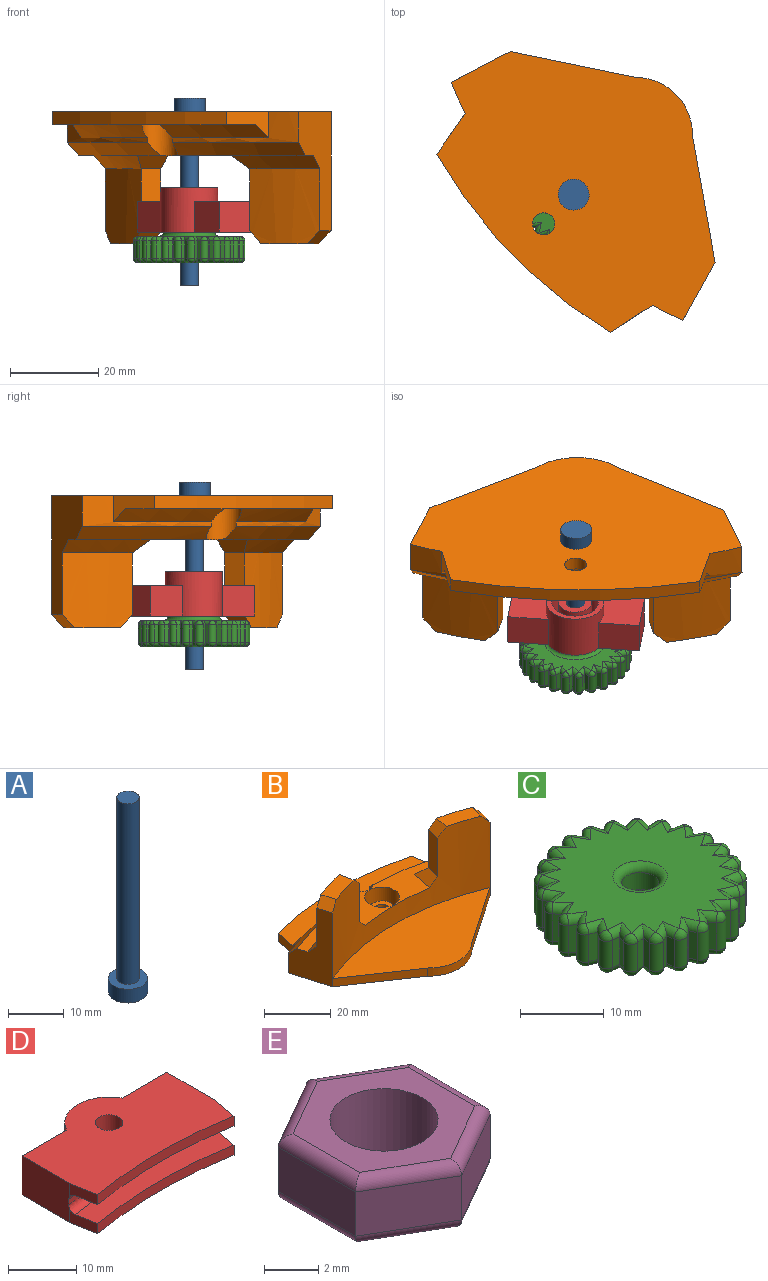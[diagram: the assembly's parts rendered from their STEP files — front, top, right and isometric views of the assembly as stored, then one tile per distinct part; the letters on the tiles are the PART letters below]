
ASSEMBLY  parts=5 mates=4
PART A: 5 faces, bbox 7x7x42.5 mm
  f0: cylinder r=2mm len=39.5mm, axis (0,0,-1), area 496.4mm2, adj f3,f4
  f1: cylinder r=3.5mm len=7mm, axis (0,0,1), area 66mm2, adj f2,f3
  f2: plane 7x7mm, normal (0,0,-1), area 38.5mm2, adj f1
  f3: plane 7x7mm, normal (0,0,1), area 25.9mm2, adj f0,f1
  f4: plane 4x4mm, normal (0,0,1), area 12.6mm2, adj f0
PART B: 40 faces, bbox 75.9x52x30 mm
  f0: cylinder r=5.25mm len=10.5mm, axis (0,0,-1), area 230.9mm2, adj f3,f26
  f1: cylinder r=2mm len=6mm, axis (0,0,-1), area 75.4mm2, adj f17,f27
  f2: cylinder r=3.75mm len=7.5mm, axis (0,0,-1), area 70.7mm2, adj f26,f27
  f3: plane 73.58x13.09mm, normal (0,0,1), area 429.3mm2, adj f0,f7,f11,f18,f19,f30,f31,f36
  f4: plane 66.65x27mm, normal (0,0,1), area 1048.8mm2, adj f8,f9,f10,f18
  f5: plane 11.08x6.03mm, normal (-0.98,0.19,0), area 38.9mm2, adj f6,f14,f16,f17,f28
  f6: cylinder r=100mm len=33.66mm, axis (0,0,-1), area 80.9mm2, adj f5,f7,f17,f19,f28,f31
  f7: plane 27.01x14.45mm, normal (-0.96,-0.29,0), area 240.5mm2, adj f3,f6,f8,f17,f18,f24,f31,f32
  f8: plane 24.01x16.26mm, normal (-0.56,-0.83,0), area 87mm2, adj f4,f7,f9,f17
  f9: cylinder r=13mm len=18.64mm, axis (0,0,-1), area 62.3mm2, adj f4,f8,f10,f17
  f10: plane 24.01x16.26mm, normal (0.56,-0.83,0), area 87mm2, adj f4,f9,f11,f17
  f11: plane 27.01x14.45mm, normal (0.96,-0.29,0), area 240.5mm2, adj f3,f10,f12,f17,f18,f20,f30,f33
  f12: cylinder r=100mm len=33.66mm, axis (0,0,-1), area 80.9mm2, adj f11,f13,f17,f19,f29,f30
  f13: plane 11.08x6.03mm, normal (0.98,0.19,0), area 38.9mm2, adj f12,f14,f16,f17,f29
  f14: cylinder r=110mm len=56.42mm, axis (0,0,-1), area 171.2mm2, adj f5,f13,f16,f17
  f15: cylinder r=2.5mm len=5mm, axis (0,0,-1), area 47.1mm2, adj f16,f17
  f16: plane 59.48x14mm, normal (0,0,1), area 437.7mm2, adj f5,f13,f14,f15,f19,f28,f29
  f17: plane 75.31x52mm, normal (0,0,-1), area 2703.4mm2, adj f1,f5,f6,f7,f8,f9,f10,f11
  f18: cylinder r=85mm len=66.65mm, axis (0,0,-1), area 1172mm2, adj f3,f4,f7,f11,f21,f22,f23,f25
  f19: cylinder r=4mm len=8mm, axis (0,0,-1), area 86.9mm2, adj f3,f6,f12,f16,f28,f29,f30,f31
  f20: cylinder r=90.24mm len=17.3mm, axis (0,0,-1), area 298.9mm2, adj f11,f21,f22,f33,f35,f39
  f21: plane 14x5.13mm, normal (-0.98,0.21,0), area 73.4mm2, adj f18,f20,f35,f38
  f22: plane 12.66x8.56mm, normal (0,0,1), area 62.4mm2, adj f18,f20,f33,f35
  f23: plane 14x5.13mm, normal (0.98,0.21,0), area 73.4mm2, adj f18,f24,f34,f37
  f24: cylinder r=90.24mm len=17.01mm, axis (0,0,-1), area 293.9mm2, adj f7,f23,f25,f32,f34,f36
  f25: plane 12.37x8.5mm, normal (0,0,1), area 60.8mm2, adj f18,f24,f32,f34
  f26: plane 10.5x10.5mm, normal (0,0,1), area 42.4mm2, adj f0,f2
  f27: plane 7.5x7.5mm, normal (0,0,1), area 31.6mm2, adj f1,f2
  f28: cone r=103mm half-angle=45deg, axis (0,0,-1), area 114.2mm2, adj f5,f6,f16,f19
  f29: cone r=103mm half-angle=45deg, axis (0,0,-1), area 114.2mm2, adj f12,f13,f16,f19
  f30: cone r=97mm half-angle=45deg, axis (0,0,-1), area 146.8mm2, adj f3,f11,f12,f19
  f31: cone r=97mm half-angle=45deg, axis (0,0,-1), area 146.8mm2, adj f3,f6,f7,f19
  f32: plane 6.17x4.31mm, normal (-0.68,-0.2,0.71), area 22.3mm2, adj f7,f18,f24,f25
  f33: plane 6.17x4.31mm, normal (0.68,-0.2,0.71), area 22.3mm2, adj f11,f18,f20,f22
  f34: plane 5.77x4.02mm, normal (0.69,0.15,0.71), area 22.3mm2, adj f18,f23,f24,f25
  f35: plane 5.76x4.02mm, normal (-0.69,0.15,0.71), area 22.3mm2, adj f18,f20,f21,f22
  f36: cone r=93.24mm half-angle=45deg, axis (0,0,-1), area 82.4mm2, adj f3,f7,f24,f37
  f37: plane 8.65x4.08mm, normal (0.69,0.15,0.71), area 28.6mm2, adj f3,f18,f23,f36
  f38: plane 8.64x4.09mm, normal (-0.69,0.15,0.71), area 28.6mm2, adj f3,f18,f21,f39
  f39: cone r=93.24mm half-angle=45deg, axis (0,0,-1), area 83.7mm2, adj f3,f11,f20,f38
PART C: 238 faces, bbox 25.3x25.3x7.7 mm
  f0: plane 4x0.99mm, normal (0.44,0.9,0), area 4.4mm2, adj f1,f74,f157,f232
  f1: plane 4x0.82mm, normal (0.74,-0.67,0), area 4.4mm2, adj f0,f2,f155,f230
  f2: cylinder r=1mm len=4mm, axis (0,0,-1), area 8.4mm2, adj f1,f3,f153,f228
  f3: plane 4x1.08mm, normal (0.21,0.98,0), area 4.4mm2, adj f2,f4,f151,f226
  f4: plane 4x0.98mm, normal (0.89,-0.46,0), area 4.4mm2, adj f3,f5,f149,f224
  f5: cylinder r=1mm len=4mm, axis (0,0,-1), area 8.4mm2, adj f4,f6,f147,f222
  f6: plane 4x1.11mm, normal (-0.04,1,0), area 4.4mm2, adj f5,f7,f145,f220
  f7: plane 4x1.08mm, normal (0.97,-0.23,0), area 4.4mm2, adj f6,f8,f143,f218
  f8: cylinder r=1mm len=4mm, axis (0,0,-1), area 8.4mm2, adj f7,f9,f141,f216
  f9: plane 4x1.06mm, normal (-0.29,0.96,0), area 4.4mm2, adj f8,f10,f139,f214
  f10: plane 4x1.11mm, normal (1,0.02,0), area 4.4mm2, adj f9,f11,f137,f212
  f11: cylinder r=1mm len=4mm, axis (0,0,-1), area 8.4mm2, adj f10,f12,f135,f210
  f12: plane 4x0.95mm, normal (-0.52,0.86,0), area 4.4mm2, adj f11,f13,f133,f208
  f13: plane 4x1.07mm, normal (0.96,0.27,0), area 4.4mm2, adj f12,f14,f131,f206
  f14: cylinder r=1mm len=4mm, axis (0,0,-1), area 8.4mm2, adj f13,f15,f129,f204
  f15: plane 4x0.79mm, normal (-0.71,0.7,0), area 4.4mm2, adj f14,f16,f127,f202
  f16: plane 4x0.96mm, normal (0.87,0.5,0), area 4.4mm2, adj f15,f17,f125,f200
  f17: cylinder r=1mm len=4mm, axis (0,0,-1), area 8.4mm2, adj f16,f18,f123,f198
  f18: plane 4x0.96mm, normal (-0.87,0.5,0), area 4.4mm2, adj f17,f19,f121,f196
  f19: plane 4x0.79mm, normal (0.71,0.7,0), area 4.4mm2, adj f18,f20,f119,f194
  f20: cylinder r=1mm len=4mm, axis (0,0,-1), area 8.4mm2, adj f19,f21,f117,f192
  f21: plane 4x1.07mm, normal (-0.96,0.27,0), area 4.4mm2, adj f20,f22,f115,f190
  f22: plane 4x0.95mm, normal (0.52,0.86,0), area 4.4mm2, adj f21,f23,f113,f188
  f23: cylinder r=1mm len=4mm, axis (0,0,-1), area 8.4mm2, adj f22,f24,f111,f186
  f24: plane 4x1.11mm, normal (-1,0.02,0), area 4.4mm2, adj f23,f25,f109,f184
  f25: plane 4x1.06mm, normal (0.29,0.96,0), area 4.4mm2, adj f24,f26,f107,f182
  f26: cylinder r=1mm len=4mm, axis (0,0,-1), area 8.4mm2, adj f25,f27,f105,f180
  f27: plane 4x1.08mm, normal (-0.97,-0.23,0), area 4.4mm2, adj f26,f28,f103,f178
  f28: plane 4x1.11mm, normal (0.04,1,0), area 4.4mm2, adj f27,f29,f101,f176
  f29: cylinder r=1mm len=4mm, axis (0,0,-1), area 8.4mm2, adj f28,f30,f99,f174
  f30: plane 4x0.98mm, normal (-0.89,-0.46,0), area 4.4mm2, adj f29,f31,f97,f172
  f31: plane 4x1.08mm, normal (-0.21,0.98,0), area 4.4mm2, adj f30,f32,f95,f170
  f32: cylinder r=1mm len=4mm, axis (0,0,-1), area 8.4mm2, adj f31,f33,f93,f168
  f33: plane 4x0.82mm, normal (-0.74,-0.67,0), area 4.4mm2, adj f32,f34,f91,f166
  f34: plane 4x0.99mm, normal (-0.44,0.9,0), area 4.4mm2, adj f33,f35,f89,f164
  f35: cylinder r=1mm len=4mm, axis (0,0,-1), area 8.4mm2, adj f34,f36,f87,f162
  f36: plane 4x0.92mm, normal (-0.55,-0.83,0), area 4.4mm2, adj f35,f37,f88,f163
  f37: plane 4x0.84mm, normal (-0.65,0.76,0), area 4.4mm2, adj f36,f38,f90,f165
  f38: cylinder r=1mm len=4mm, axis (0,0,-1), area 8.4mm2, adj f37,f39,f92,f167
  f39: plane 4x1.05mm, normal (-0.33,-0.94,0), area 4.4mm2, adj f38,f40,f94,f169
  f40: plane 4x0.91mm, normal (-0.82,0.57,0), area 4.4mm2, adj f39,f41,f96,f171
  f41: cylinder r=1mm len=4mm, axis (0,0,-1), area 8.4mm2, adj f40,f42,f98,f173
  f42: plane 4x1.1mm, normal (-0.08,-1,0), area 4.4mm2, adj f41,f43,f100,f175
  f43: plane 4x1.04mm, normal (-0.94,0.35,0), area 4.4mm2, adj f42,f44,f102,f177
  f44: cylinder r=1mm len=4mm, axis (0,0,-1), area 8.4mm2, adj f43,f45,f104,f179
  f45: plane 4x1.09mm, normal (0.17,-0.99,0), area 4.4mm2, adj f44,f46,f106,f181
  f46: plane 4x1.1mm, normal (-0.99,0.1,0), area 4.4mm2, adj f45,f47,f108,f183
  f47: cylinder r=1mm len=4mm, axis (0,0,-1), area 8.4mm2, adj f46,f48,f110,f185
  f48: plane 4x1.01mm, normal (0.41,-0.91,0), area 4.4mm2, adj f47,f49,f112,f187
  f49: plane 4x1.1mm, normal (-0.99,-0.15,0), area 4.4mm2, adj f48,f50,f114,f189
  f50: cylinder r=1mm len=4mm, axis (0,0,-1), area 8.4mm2, adj f49,f51,f116,f191
  f51: plane 4x0.87mm, normal (0.62,-0.78,0), area 4.4mm2, adj f50,f52,f118,f193
  f52: plane 4x1.02mm, normal (-0.92,-0.39,0), area 4.4mm2, adj f51,f53,f120,f195
  f53: cylinder r=1mm len=4mm, axis (0,0,-1), area 8.4mm2, adj f52,f54,f122,f197
  f54: plane 4x0.88mm, normal (0.8,-0.6,0), area 4.4mm2, adj f53,f55,f124,f199
  f55: plane 4x0.88mm, normal (-0.8,-0.6,0), area 4.4mm2, adj f54,f56,f126,f201
  f56: cylinder r=1mm len=4mm, axis (0,0,-1), area 8.4mm2, adj f55,f57,f128,f203
  f57: plane 4x1.02mm, normal (0.92,-0.39,0), area 4.4mm2, adj f56,f58,f130,f205
  f58: plane 4x0.87mm, normal (-0.62,-0.78,0), area 4.4mm2, adj f57,f59,f132,f207
  f59: cylinder r=1mm len=4mm, axis (0,0,-1), area 8.4mm2, adj f58,f60,f134,f209
  f60: plane 4x1.1mm, normal (0.99,-0.15,0), area 4.4mm2, adj f59,f61,f136,f211
  f61: plane 4x1.01mm, normal (-0.41,-0.91,0), area 4.4mm2, adj f60,f62,f138,f213
  f62: cylinder r=1mm len=4mm, axis (0,0,-1), area 8.4mm2, adj f61,f63,f140,f215
  f63: plane 4x1.1mm, normal (0.99,0.1,0), area 4.4mm2, adj f62,f64,f142,f217
  f64: plane 4x1.09mm, normal (-0.17,-0.99,0), area 4.4mm2, adj f63,f65,f144,f219
  f65: cylinder r=1mm len=4mm, axis (0,0,-1), area 8.4mm2, adj f64,f66,f146,f221
  f66: plane 4x1.04mm, normal (0.94,0.35,0), area 4.4mm2, adj f65,f67,f148,f223
  f67: plane 4x1.1mm, normal (0.08,-1,0), area 4.4mm2, adj f66,f68,f150,f225
  f68: cylinder r=1mm len=4mm, axis (0,0,-1), area 8.4mm2, adj f67,f69,f152,f227
  f69: plane 4x0.91mm, normal (0.82,0.57,0), area 4.4mm2, adj f68,f70,f154,f229
  f70: plane 4x1.05mm, normal (0.33,-0.94,0), area 4.4mm2, adj f69,f71,f156,f231
  f71: cylinder r=1mm len=4mm, axis (0,0,-1), area 8.4mm2, adj f70,f72,f158,f233
  f72: plane 4x0.84mm, normal (0.65,0.76,0), area 4.4mm2, adj f71,f73,f160,f235
  f73: plane 4x0.92mm, normal (0.55,-0.83,0), area 4.4mm2, adj f72,f74,f161,f236
  f74: cylinder r=1mm len=4mm, axis (0,0,-1), area 8.4mm2, adj f0,f73,f159,f234
  f75: cylinder r=2.25mm len=4.5mm, axis (0,0,-1), area 35.3mm2, adj f84,f237
  f76: plane 23.34x23.3mm, normal (0,0,1), area 321.2mm2, adj f163,f164,f165,f166,f169,f170,f171,f172
  f77: plane 23.34x23.3mm, normal (0,0,-1), area 207.8mm2, adj f86,f88,f89,f90,f91,f94,f95,f96
  f78: plane 3.79x3.5mm, normal (-0.87,-0.49,0), area 15.2mm2, adj f79,f83,f84,f85
  f79: plane 4.33x3.5mm, normal (-0.02,-1,0), area 15.2mm2, adj f78,f80,f84,f85
  f80: plane 3.71x3.5mm, normal (0.86,-0.51,0), area 15.2mm2, adj f79,f81,f84,f85
  f81: plane 3.79x3.5mm, normal (0.87,0.49,0), area 15.2mm2, adj f80,f82,f84,f85
  f82: plane 4.33x3.5mm, normal (0.02,1,0), area 15.2mm2, adj f81,f83,f84,f85
  f83: plane 3.71x3.5mm, normal (-0.86,0.51,0), area 15.2mm2, adj f78,f82,f84,f85
  f84: plane 8.66x7.57mm, normal (0,0,-1), area 32.8mm2, adj f75,f78,f79,f80,f81,f82,f83
  f85: plane 11.66x11.66mm, normal (0,0,-1), area 58.1mm2, adj f78,f79,f80,f81,f82,f83,f86
  f86: torus R=6.83mm, axis (0,0,1), area 61.1mm2, adj f77,f85
  f87: sphere r=1mm, area 2.1mm2, adj f35,f88,f89
  f88: cylinder r=1mm len=2.57mm, axis (0.83,-0.55,0), area 2.5mm2, adj f36,f77,f87,f90
  f89: cylinder r=1mm len=2.62mm, axis (-0.9,-0.44,0), area 2.5mm2, adj f34,f77,f87,f91
  f90: cylinder r=1mm len=2.49mm, axis (-0.76,-0.65,0), area 2.5mm2, adj f37,f77,f88,f92
  f91: cylinder r=1mm len=2.47mm, axis (0.67,-0.74,0), area 2.5mm2, adj f33,f77,f89,f93
  f92: sphere r=1mm, area 2.1mm2, adj f38,f90,f94
  f93: sphere r=1mm, area 2.1mm2, adj f32,f91,f95
  f94: cylinder r=1mm len=2.62mm, axis (0.94,-0.33,0), area 2.5mm2, adj f39,f77,f92,f96
  f95: cylinder r=1mm len=2.58mm, axis (-0.98,-0.21,0), area 2.5mm2, adj f31,f77,f93,f97
  f96: cylinder r=1mm len=2.56mm, axis (-0.57,-0.82,0), area 2.5mm2, adj f40,f77,f94,f98
  f97: cylinder r=1mm len=2.61mm, axis (0.46,-0.89,0), area 2.5mm2, adj f30,f77,f95,f99
  f98: sphere r=1mm, area 2.1mm2, adj f41,f96,f100
  f99: sphere r=1mm, area 2.1mm2, adj f29,f97,f101
  f100: cylinder r=1mm len=2.5mm, axis (1,-0.08,0), area 2.5mm2, adj f42,f77,f98,f102
  f101: cylinder r=1mm len=2.46mm, axis (-1,0.04,0), area 2.5mm2, adj f28,f77,f99,f103
  f102: cylinder r=1mm len=2.62mm, axis (-0.35,-0.94,0), area 2.5mm2, adj f43,f77,f100,f104
  f103: cylinder r=1mm len=2.59mm, axis (0.23,-0.97,0), area 2.5mm2, adj f27,f77,f101,f105
  f104: sphere r=1mm, area 2.1mm2, adj f44,f102,f106
  f105: sphere r=1mm, area 2.1mm2, adj f26,f103,f107
  f106: cylinder r=1mm len=2.56mm, axis (0.99,0.17,0), area 2.5mm2, adj f45,f77,f104,f108
  f107: cylinder r=1mm len=2.61mm, axis (-0.96,0.29,0), area 2.5mm2, adj f25,f77,f105,f109
  f108: cylinder r=1mm len=2.52mm, axis (-0.1,-0.99,0), area 2.5mm2, adj f46,f77,f106,f110
  f109: cylinder r=1mm len=2.44mm, axis (-0.02,-1,0), area 2.5mm2, adj f24,f77,f107,f111
  f110: sphere r=1mm, area 2.1mm2, adj f47,f108,f112
  f111: sphere r=1mm, area 2.1mm2, adj f23,f109,f113
  f112: cylinder r=1mm len=2.62mm, axis (0.91,0.41,0), area 2.5mm2, adj f48,f77,f110,f114
  f113: cylinder r=1mm len=2.59mm, axis (-0.86,0.52,0), area 2.5mm2, adj f22,f77,f111,f115
  f114: cylinder r=1mm len=2.54mm, axis (0.15,-0.99,0), area 2.5mm2, adj f49,f77,f112,f116
  f115: cylinder r=1mm len=2.6mm, axis (-0.27,-0.96,0), area 2.5mm2, adj f21,f77,f113,f117
  f116: sphere r=1mm, area 2.1mm2, adj f50,f114,f118
  f117: sphere r=1mm, area 2.1mm2, adj f20,f115,f119
  f118: cylinder r=1mm len=2.52mm, axis (0.78,0.62,0), area 2.5mm2, adj f51,f77,f116,f120
  f119: cylinder r=1mm len=2.43mm, axis (-0.7,0.71,0), area 2.5mm2, adj f19,f77,f117,f121
  f120: cylinder r=1mm len=2.62mm, axis (0.39,-0.92,0), area 2.5mm2, adj f52,f77,f118,f122
  f121: cylinder r=1mm len=2.6mm, axis (-0.5,-0.87,0), area 2.5mm2, adj f18,f77,f119,f123
  f122: sphere r=1mm, area 2.1mm2, adj f53,f120,f124
  f123: sphere r=1mm, area 2.1mm2, adj f17,f121,f125
  f124: cylinder r=1mm len=2.54mm, axis (0.6,0.8,0), area 2.5mm2, adj f54,f77,f122,f126
  f125: cylinder r=1mm len=2.6mm, axis (-0.5,0.87,0), area 2.5mm2, adj f16,f77,f123,f127
  f126: cylinder r=1mm len=2.54mm, axis (0.6,-0.8,0), area 2.5mm2, adj f55,f77,f124,f128
  f127: cylinder r=1mm len=2.43mm, axis (-0.7,-0.71,0), area 2.5mm2, adj f15,f77,f125,f129
  f128: sphere r=1mm, area 2.1mm2, adj f56,f126,f130
  f129: sphere r=1mm, area 2.1mm2, adj f14,f127,f131
  f130: cylinder r=1mm len=2.62mm, axis (0.39,0.92,0), area 2.5mm2, adj f57,f77,f128,f132
  f131: cylinder r=1mm len=2.6mm, axis (-0.27,0.96,0), area 2.5mm2, adj f13,f77,f129,f133
  f132: cylinder r=1mm len=2.52mm, axis (0.78,-0.62,0), area 2.5mm2, adj f58,f77,f130,f134
  f133: cylinder r=1mm len=2.59mm, axis (-0.86,-0.52,0), area 2.5mm2, adj f12,f77,f131,f135
  f134: sphere r=1mm, area 2.1mm2, adj f59,f132,f136
  f135: sphere r=1mm, area 2.1mm2, adj f11,f133,f137
  f136: cylinder r=1mm len=2.54mm, axis (0.15,0.99,0), area 2.5mm2, adj f60,f77,f134,f138
  f137: cylinder r=1mm len=2.44mm, axis (-0.02,1,0), area 2.5mm2, adj f10,f77,f135,f139
  f138: cylinder r=1mm len=2.62mm, axis (0.91,-0.41,0), area 2.5mm2, adj f61,f77,f136,f140
  f139: cylinder r=1mm len=2.61mm, axis (-0.96,-0.29,0), area 2.5mm2, adj f9,f77,f137,f141
  f140: sphere r=1mm, area 2.1mm2, adj f62,f138,f142
  f141: sphere r=1mm, area 2.1mm2, adj f8,f139,f143
  f142: cylinder r=1mm len=2.52mm, axis (-0.1,0.99,0), area 2.5mm2, adj f63,f77,f140,f144
  f143: cylinder r=1mm len=2.59mm, axis (0.23,0.97,0), area 2.5mm2, adj f7,f77,f141,f145
  f144: cylinder r=1mm len=2.56mm, axis (0.99,-0.17,0), area 2.5mm2, adj f64,f77,f142,f146
  f145: cylinder r=1mm len=2.46mm, axis (-1,-0.04,0), area 2.5mm2, adj f6,f77,f143,f147
  f146: sphere r=1mm, area 2.1mm2, adj f65,f144,f148
  f147: sphere r=1mm, area 2.1mm2, adj f5,f145,f149
  f148: cylinder r=1mm len=2.62mm, axis (-0.35,0.94,0), area 2.5mm2, adj f66,f77,f146,f150
  f149: cylinder r=1mm len=2.61mm, axis (0.46,0.89,0), area 2.5mm2, adj f4,f77,f147,f151
  f150: cylinder r=1mm len=2.5mm, axis (1,0.08,0), area 2.5mm2, adj f67,f77,f148,f152
  f151: cylinder r=1mm len=2.58mm, axis (-0.98,0.21,0), area 2.5mm2, adj f3,f77,f149,f153
  f152: sphere r=1mm, area 2.1mm2, adj f68,f150,f154
  f153: sphere r=1mm, area 2.1mm2, adj f2,f151,f155
  f154: cylinder r=1mm len=2.56mm, axis (-0.57,0.82,0), area 2.5mm2, adj f69,f77,f152,f156
  f155: cylinder r=1mm len=2.47mm, axis (0.67,0.74,0), area 2.5mm2, adj f1,f77,f153,f157
  f156: cylinder r=1mm len=2.62mm, axis (0.94,0.33,0), area 2.5mm2, adj f70,f77,f154,f158
  f157: cylinder r=1mm len=2.62mm, axis (-0.9,0.44,0), area 2.5mm2, adj f0,f77,f155,f159
  f158: sphere r=1mm, area 2.1mm2, adj f71,f156,f160
  f159: sphere r=1mm, area 2.1mm2, adj f74,f157,f161
  f160: cylinder r=1mm len=2.49mm, axis (-0.76,0.65,0), area 2.5mm2, adj f72,f77,f158,f161
  f161: cylinder r=1mm len=2.57mm, axis (0.83,0.55,0), area 2.5mm2, adj f73,f77,f159,f160
  f162: sphere r=1mm, area 2.1mm2, adj f35,f163,f164
  f163: cylinder r=1mm len=2.57mm, axis (-0.83,0.55,0), area 2.5mm2, adj f36,f76,f162,f165
  f164: cylinder r=1mm len=2.62mm, axis (0.9,0.44,0), area 2.5mm2, adj f34,f76,f162,f166
  f165: cylinder r=1mm len=2.49mm, axis (0.76,0.65,0), area 2.5mm2, adj f37,f76,f163,f167
  f166: cylinder r=1mm len=2.47mm, axis (-0.67,0.74,0), area 2.5mm2, adj f33,f76,f164,f168
  f167: sphere r=1mm, area 2.1mm2, adj f38,f165,f169
  f168: sphere r=1mm, area 2.1mm2, adj f32,f166,f170
  f169: cylinder r=1mm len=2.62mm, axis (-0.94,0.33,0), area 2.5mm2, adj f39,f76,f167,f171
  f170: cylinder r=1mm len=2.58mm, axis (0.98,0.21,0), area 2.5mm2, adj f31,f76,f168,f172
  f171: cylinder r=1mm len=2.56mm, axis (0.57,0.82,0), area 2.5mm2, adj f40,f76,f169,f173
  f172: cylinder r=1mm len=2.61mm, axis (-0.46,0.89,0), area 2.5mm2, adj f30,f76,f170,f174
  f173: sphere r=1mm, area 2.1mm2, adj f41,f171,f175
  f174: sphere r=1mm, area 2.1mm2, adj f29,f172,f176
  f175: cylinder r=1mm len=2.5mm, axis (-1,0.08,0), area 2.5mm2, adj f42,f76,f173,f177
  f176: cylinder r=1mm len=2.46mm, axis (1,-0.04,0), area 2.5mm2, adj f28,f76,f174,f178
  f177: cylinder r=1mm len=2.62mm, axis (0.35,0.94,0), area 2.5mm2, adj f43,f76,f175,f179
  f178: cylinder r=1mm len=2.59mm, axis (-0.23,0.97,0), area 2.5mm2, adj f27,f76,f176,f180
  f179: sphere r=1mm, area 2.1mm2, adj f44,f177,f181
  f180: sphere r=1mm, area 2.1mm2, adj f26,f178,f182
  f181: cylinder r=1mm len=2.56mm, axis (-0.99,-0.17,0), area 2.5mm2, adj f45,f76,f179,f183
  f182: cylinder r=1mm len=2.61mm, axis (0.96,-0.29,0), area 2.5mm2, adj f25,f76,f180,f184
  f183: cylinder r=1mm len=2.52mm, axis (0.1,0.99,0), area 2.5mm2, adj f46,f76,f181,f185
  f184: cylinder r=1mm len=2.44mm, axis (0.02,1,0), area 2.5mm2, adj f24,f76,f182,f186
  f185: sphere r=1mm, area 2.1mm2, adj f47,f183,f187
  f186: sphere r=1mm, area 2.1mm2, adj f23,f184,f188
  f187: cylinder r=1mm len=2.62mm, axis (-0.91,-0.41,0), area 2.5mm2, adj f48,f76,f185,f189
  f188: cylinder r=1mm len=2.59mm, axis (0.86,-0.52,0), area 2.5mm2, adj f22,f76,f186,f190
  f189: cylinder r=1mm len=2.54mm, axis (-0.15,0.99,0), area 2.5mm2, adj f49,f76,f187,f191
  f190: cylinder r=1mm len=2.6mm, axis (0.27,0.96,0), area 2.5mm2, adj f21,f76,f188,f192
  f191: sphere r=1mm, area 2.1mm2, adj f50,f189,f193
  f192: sphere r=1mm, area 2.1mm2, adj f20,f190,f194
  f193: cylinder r=1mm len=2.52mm, axis (-0.78,-0.62,0), area 2.5mm2, adj f51,f76,f191,f195
  f194: cylinder r=1mm len=2.43mm, axis (0.7,-0.71,0), area 2.5mm2, adj f19,f76,f192,f196
  f195: cylinder r=1mm len=2.62mm, axis (-0.39,0.92,0), area 2.5mm2, adj f52,f76,f193,f197
  f196: cylinder r=1mm len=2.6mm, axis (0.5,0.87,0), area 2.5mm2, adj f18,f76,f194,f198
  f197: sphere r=1mm, area 2.1mm2, adj f53,f195,f199
  f198: sphere r=1mm, area 2.1mm2, adj f17,f196,f200
  f199: cylinder r=1mm len=2.54mm, axis (-0.6,-0.8,0), area 2.5mm2, adj f54,f76,f197,f201
  f200: cylinder r=1mm len=2.6mm, axis (0.5,-0.87,0), area 2.5mm2, adj f16,f76,f198,f202
  f201: cylinder r=1mm len=2.54mm, axis (-0.6,0.8,0), area 2.5mm2, adj f55,f76,f199,f203
  f202: cylinder r=1mm len=2.43mm, axis (0.7,0.71,0), area 2.5mm2, adj f15,f76,f200,f204
  f203: sphere r=1mm, area 2.1mm2, adj f56,f201,f205
  f204: sphere r=1mm, area 2.1mm2, adj f14,f202,f206
  f205: cylinder r=1mm len=2.62mm, axis (-0.39,-0.92,0), area 2.5mm2, adj f57,f76,f203,f207
  f206: cylinder r=1mm len=2.6mm, axis (0.27,-0.96,0), area 2.5mm2, adj f13,f76,f204,f208
  f207: cylinder r=1mm len=2.52mm, axis (-0.78,0.62,0), area 2.5mm2, adj f58,f76,f205,f209
  f208: cylinder r=1mm len=2.59mm, axis (0.86,0.52,0), area 2.5mm2, adj f12,f76,f206,f210
  f209: sphere r=1mm, area 2.1mm2, adj f59,f207,f211
  f210: sphere r=1mm, area 2.1mm2, adj f11,f208,f212
  f211: cylinder r=1mm len=2.54mm, axis (-0.15,-0.99,0), area 2.5mm2, adj f60,f76,f209,f213
  f212: cylinder r=1mm len=2.44mm, axis (0.02,-1,0), area 2.5mm2, adj f10,f76,f210,f214
  f213: cylinder r=1mm len=2.62mm, axis (-0.91,0.41,0), area 2.5mm2, adj f61,f76,f211,f215
  f214: cylinder r=1mm len=2.61mm, axis (0.96,0.29,0), area 2.5mm2, adj f9,f76,f212,f216
  f215: sphere r=1mm, area 2.1mm2, adj f62,f213,f217
  f216: sphere r=1mm, area 2.1mm2, adj f8,f214,f218
  f217: cylinder r=1mm len=2.52mm, axis (0.1,-0.99,0), area 2.5mm2, adj f63,f76,f215,f219
  f218: cylinder r=1mm len=2.59mm, axis (-0.23,-0.97,0), area 2.5mm2, adj f7,f76,f216,f220
  f219: cylinder r=1mm len=2.56mm, axis (-0.99,0.17,0), area 2.5mm2, adj f64,f76,f217,f221
  f220: cylinder r=1mm len=2.46mm, axis (1,0.04,0), area 2.5mm2, adj f6,f76,f218,f222
  f221: sphere r=1mm, area 2.1mm2, adj f65,f219,f223
  f222: sphere r=1mm, area 2.1mm2, adj f5,f220,f224
  f223: cylinder r=1mm len=2.62mm, axis (0.35,-0.94,0), area 2.5mm2, adj f66,f76,f221,f225
  f224: cylinder r=1mm len=2.61mm, axis (-0.46,-0.89,0), area 2.5mm2, adj f4,f76,f222,f226
  f225: cylinder r=1mm len=2.5mm, axis (-1,-0.08,0), area 2.5mm2, adj f67,f76,f223,f227
  f226: cylinder r=1mm len=2.58mm, axis (0.98,-0.21,0), area 2.5mm2, adj f3,f76,f224,f228
  f227: sphere r=1mm, area 2.1mm2, adj f68,f225,f229
  f228: sphere r=1mm, area 2.1mm2, adj f2,f226,f230
  f229: cylinder r=1mm len=2.56mm, axis (0.57,-0.82,0), area 2.5mm2, adj f69,f76,f227,f231
  f230: cylinder r=1mm len=2.47mm, axis (-0.67,-0.74,0), area 2.5mm2, adj f1,f76,f228,f232
  f231: cylinder r=1mm len=2.62mm, axis (-0.94,-0.33,0), area 2.5mm2, adj f70,f76,f229,f233
  f232: cylinder r=1mm len=2.62mm, axis (0.9,-0.44,0), area 2.5mm2, adj f0,f76,f230,f234
  f233: sphere r=1mm, area 2.1mm2, adj f71,f231,f235
  f234: sphere r=1mm, area 2.1mm2, adj f74,f232,f236
  f235: cylinder r=1mm len=2.49mm, axis (0.76,-0.65,0), area 2.5mm2, adj f72,f76,f233,f236
  f236: cylinder r=1mm len=2.57mm, axis (-0.83,-0.55,0), area 2.5mm2, adj f73,f76,f234,f235
  f237: torus R=3.25mm, axis (0,0,1), area 25.8mm2, adj f75,f76
PART D: 25 faces, bbox 30.6x18.3x10 mm
  f0: plane 4.92x2.34mm, normal (-0.98,-0.18,0), area 9.2mm2, adj f1,f5,f13,f21,f23
  f1: cylinder r=80mm len=28.24mm, axis (0,0,-1), area 51.1mm2, adj f0,f2,f13,f21
  f2: plane 4.92x2.34mm, normal (0.98,-0.18,0), area 9.2mm2, adj f1,f9,f13,f21,f23
  f3: cylinder r=6.5mm len=13mm, axis (0,0,-1), area 199.7mm2, adj f4,f10,f12,f13,f17,f18
  f4: plane 9.26x7mm, normal (0,1,0), area 64.9mm2, adj f3,f5,f12,f13
  f5: plane 9.91x7.02mm, normal (-1,0,0), area 68.9mm2, adj f0,f4,f6,f12,f13,f22,f23,f24
  f6: plane 4.92x2.34mm, normal (-0.98,-0.18,0), area 9.2mm2, adj f5,f7,f12,f20,f24
  f7: cylinder r=80mm len=28.24mm, axis (0,0,-1), area 51.1mm2, adj f6,f8,f12,f20
  f8: plane 4.92x2.34mm, normal (0.98,-0.18,0), area 9.2mm2, adj f7,f9,f12,f20,f24
  f9: plane 9.91x7.02mm, normal (1,0,0), area 68.9mm2, adj f2,f8,f10,f12,f13,f22,f23,f24
  f10: plane 9.26x7mm, normal (0,1,0), area 64.9mm2, adj f3,f9,f12,f13
  f11: cylinder r=2mm len=10mm, axis (0,0,-1), area 125.7mm2, adj f12,f19
  f12: plane 30x18.26mm, normal (0,0,1), area 432mm2, adj f3,f4,f5,f6,f7,f8,f9,f10
  f13: plane 30x14.81mm, normal (0,0,-1), area 316.3mm2, adj f0,f1,f2,f3,f4,f5,f9,f10
  f14: cylinder r=5.25mm len=10.5mm, axis (0,0,1), area 164.9mm2, adj f16,f18
  f15: cylinder r=3.75mm len=7.5mm, axis (0,0,1), area 117.8mm2, adj f16,f19
  f16: plane 10.5x10.5mm, normal (0,0,-1), area 42.4mm2, adj f14,f15
  f17: cylinder r=85mm len=6.71mm, axis (0,0,1), area 20.1mm2, adj f3,f13,f18
  f18: plane 13x12.07mm, normal (0,0,-1), area 41.6mm2, adj f3,f14,f17
  f19: plane 7.5x7.5mm, normal (0,0,-1), area 31.6mm2, adj f11,f15
  f20: plane 29.65x5.26mm, normal (0,0,-1), area 116.4mm2, adj f6,f7,f8,f24
  f21: plane 29.65x5.26mm, normal (0,0,1), area 116.4mm2, adj f0,f1,f2,f23
  f22: cylinder r=85.2mm len=30mm, axis (0,0,-1), area 30.2mm2, adj f5,f9,f23,f24
  f23: torus R=84mm, axis (0,0,1), area 56.7mm2, adj f0,f2,f5,f9,f21,f22
  f24: torus R=84mm, axis (0,0,1), area 56.7mm2, adj f5,f6,f8,f9,f20,f22
PART E: 21 faces, bbox 7x8.1x3 mm
  f0: plane 3.51x2.03mm, normal (0.5,0.87,0), area 8.1mm2, adj f1,f5,f12,f18
  f1: plane 3.51x2.03mm, normal (-0.5,0.87,0), area 8.1mm2, adj f0,f2,f10,f16
  f2: plane 4.06x2mm, normal (-1,0,0), area 8.1mm2, adj f1,f3,f9,f15
  f3: plane 3.51x2.03mm, normal (-0.5,-0.87,0), area 8.1mm2, adj f2,f4,f11,f17
  f4: plane 3.51x2.03mm, normal (0.5,-0.87,0), area 8.1mm2, adj f3,f5,f13,f19
  f5: plane 4.06x2mm, normal (1,0,0), area 8.1mm2, adj f0,f4,f14,f20
  f6: cylinder r=2mm len=4mm, axis (0,0,1), area 37.7mm2, adj f7,f8
  f7: plane 6.96x6.03mm, normal (0,0,-1), area 18.9mm2, adj f6,f15,f16,f17,f18,f19,f20
  f8: plane 6.96x6.03mm, normal (0,0,1), area 18.9mm2, adj f6,f9,f10,f11,f12,f13,f14
  f9: cylinder r=0.5mm len=4.06mm, axis (0,-1,0), area 3mm2, adj f2,f8,f10,f11
  f10: cylinder r=0.5mm len=3.76mm, axis (-0.87,-0.5,0), area 3mm2, adj f1,f8,f9,f12
  f11: cylinder r=0.5mm len=3.76mm, axis (0.87,-0.5,0), area 3mm2, adj f3,f8,f9,f13
  f12: cylinder r=0.5mm len=3.76mm, axis (-0.87,0.5,0), area 3mm2, adj f0,f8,f10,f14
  f13: cylinder r=0.5mm len=3.76mm, axis (0.87,0.5,0), area 3mm2, adj f4,f8,f11,f14
  f14: cylinder r=0.5mm len=4.06mm, axis (0,1,0), area 3mm2, adj f5,f8,f12,f13
  f15: cylinder r=0.5mm len=4.06mm, axis (0,1,0), area 3mm2, adj f2,f7,f16,f17
  f16: cylinder r=0.5mm len=3.76mm, axis (0.87,0.5,0), area 3mm2, adj f1,f7,f15,f18
  f17: cylinder r=0.5mm len=3.76mm, axis (-0.87,0.5,0), area 3mm2, adj f3,f7,f15,f19
  f18: cylinder r=0.5mm len=3.76mm, axis (0.87,-0.5,0), area 3mm2, adj f0,f7,f16,f20
  f19: cylinder r=0.5mm len=3.76mm, axis (-0.87,-0.5,0), area 3mm2, adj f4,f7,f17,f20
  f20: cylinder r=0.5mm len=4.06mm, axis (0,-1,0), area 3mm2, adj f5,f7,f18,f19
PLACE A rot(axis=(0.93,0.38,0),180deg) t=(44.11,43.58,-2.34)mm
PLACE B rot(axis=(0.92,-0.39,0),180deg) t=(108.95,106.71,-2.34)mm
PLACE C rot(axis=(-0.33,0.94,0),180deg) t=(43.96,43.76,-30.68)mm
PLACE D rot(axis=(0.9,-0.44,0),180deg) t=(115.01,99.81,0.32)mm
PLACE E rot(axis=(0,0,-1),170.8deg) t=(44.11,43.58,-69.93)mm
MATE fastened C.f75 <-> D.f3  axis (0,0,1) through (43.96,43.76,-29.68)mm
MATE fastened E.f1 <-> C.f82  axis (0.63,-0.77,0) through (46.33,40.86,-31.43)mm
MATE fastened A.f0 <-> B.f0  axis (0,0,-1) through (44.11,43.58,-2.34)mm
MATE cylindrical A.f0 <-> E.f6  axis (0,0,1) through (44.11,43.58,-22.09)mm
